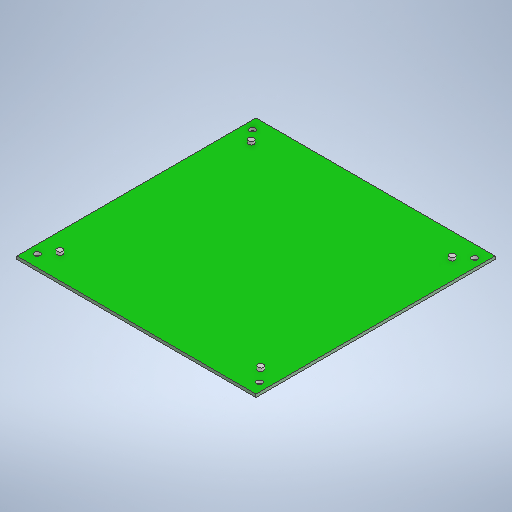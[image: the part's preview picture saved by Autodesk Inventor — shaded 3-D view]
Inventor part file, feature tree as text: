
AUTODESK INVENTOR PART (.ipt)
format: ipt  version: 2025.2 (Build 292293000, 293)  size: 253,952 bytes
history: native  units: in
note: dims shown in document units (in); Inventor stores cm internally (conversion verified against a paired STEP export)
features: extrude x3, sketch x3
ambient origin geometry x8: Origin, YZ Plane, XZ Plane, XY Plane, X Axis, Y Axis, Z Axis, Center Point
bodies: Solid1 (feature_tree)
feature tree (6):
  extrude  "Extrusion1"  Depth=5.0in
  extrude  "Extrusion2"  Depth=2.5in
  extrude  "Extrusion3"  Depth=0.0625in
  sketch  "Sketch1"  dims[d0=5.0in d1=5.0in]
  sketch  "Sketch2"  dims[d2=2.5in d3=2.5in]
  sketch  "Sketch3"  dims[d4=0.0625in d5=0.0in d6=0.12in d7=0.12in d8=0.12in d9=0.12in d10=4.5in d11=4.5in d12=0.0in d13=0.0in d14=0.0in d15=4.65in d16=0.25in d17=0.175in d18=0.0625in d19=0.0in d20=0.12in d21=0.12in d22=0.12in d23=0.12in d24=4.2in d25=4.2in d26=0.0in d27=4.0in d28=4.0in d29=0.0in d30=0.5in d31=0.4in d32=0.0625in d33=0.0in]
